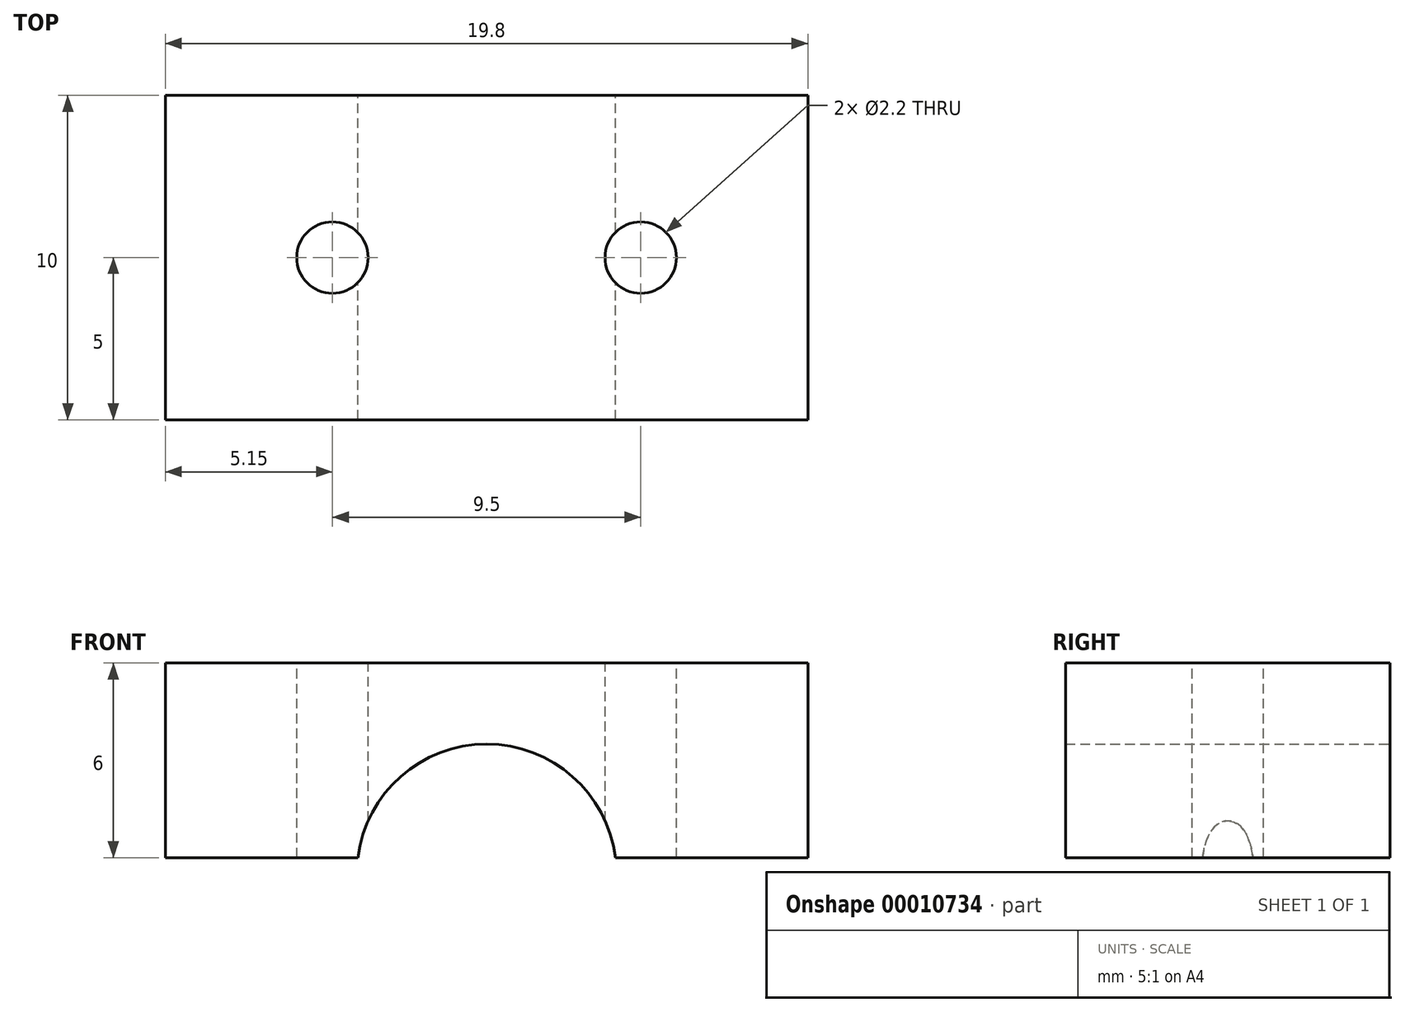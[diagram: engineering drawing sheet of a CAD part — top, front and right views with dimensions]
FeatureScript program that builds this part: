
annotation { "Feature Type Name" : "Feature", "Feature Type Description" : "" }
export const myFeature = defineFeature(function(context is Context, id is Id, definition is map)
    precondition{}
    {
        {
            var Q0;
            Q0=qCreatedBy(makeId("Front.planeOp"),FACE);
            var sketch = newSketch(context, id + "F0", { "sketchPlane" : qUnion([Q0])});
            skArc(sketch, "E0", {"start": v(3.97, 0.5) * mm, "mid": v(0, 4) * mm, "end": v(-3.97, 0.5) * mm});
            skLineSegment(sketch, "E1.bottom", {"start": v(-9.9, 0.5) * mm, "end": v(-3.97, 0.5) * mm});
            skLineSegment(sketch, "E1.top", {"start": v(-9.9, 6.5) * mm, "end": v(9.9, 6.5) * mm});
            skLineSegment(sketch, "E1.left", {"start": v(-9.9, 0.5) * mm, "end": v(-9.9, 6.5) * mm});
            skLineSegment(sketch, "E1.right", {"start": v(9.9, 0.5) * mm, "end": v(9.9, 6.5) * mm});
            skLineSegment(sketch, "E2.trimOffspring", {"start": v(3.97, 0.5) * mm, "end": v(9.9, 0.5) * mm});
            skSolve(sketch);
        }
        {
            var Q0;
            Q0 = qSketchRegion(id + "F0", true);
            extrude(context, id + "F1", {"entities" : qUnion([Q0]), "depth" : 10 * mm});
        }
        {
            var Q0;
            Q0=makeQuery(id+"F1.opExtrude","SWEPT_FACE",FACE,{"disambiguationData":[OSD([sQuery(id+"F0.wireOp",EDGE,"E1.top")])]});
            var sketch = newSketch(context, id + "F2", { "sketchPlane" : qUnion([Q0])});
            skLineSegment(sketch, "E3", {"start": v(-9.9, -5) * mm, "end": v(9.9, -5) * mm, "construction": true});
            skCircle(sketch, "E4", {"center": v(-4.75, -5) * mm, "radius": 1.1 * mm});
            skCircle(sketch, "E5.0.MirrorC", {"center": v(4.75, -5) * mm, "radius": 1.1 * mm});
            skSolve(sketch);
        }
        {
            var Q0;
            Q0 = qSketchRegion(id + "F2", true);
            extrude(context, id + "F3", {"entities" : qUnion([Q0]), "operationType" : NewBodyOperationType.REMOVE, "endBound" : BoundingType.UP_TO_NEXT, "oppositeDirection" : true, "depth" : 25 * mm});
        }
    });
